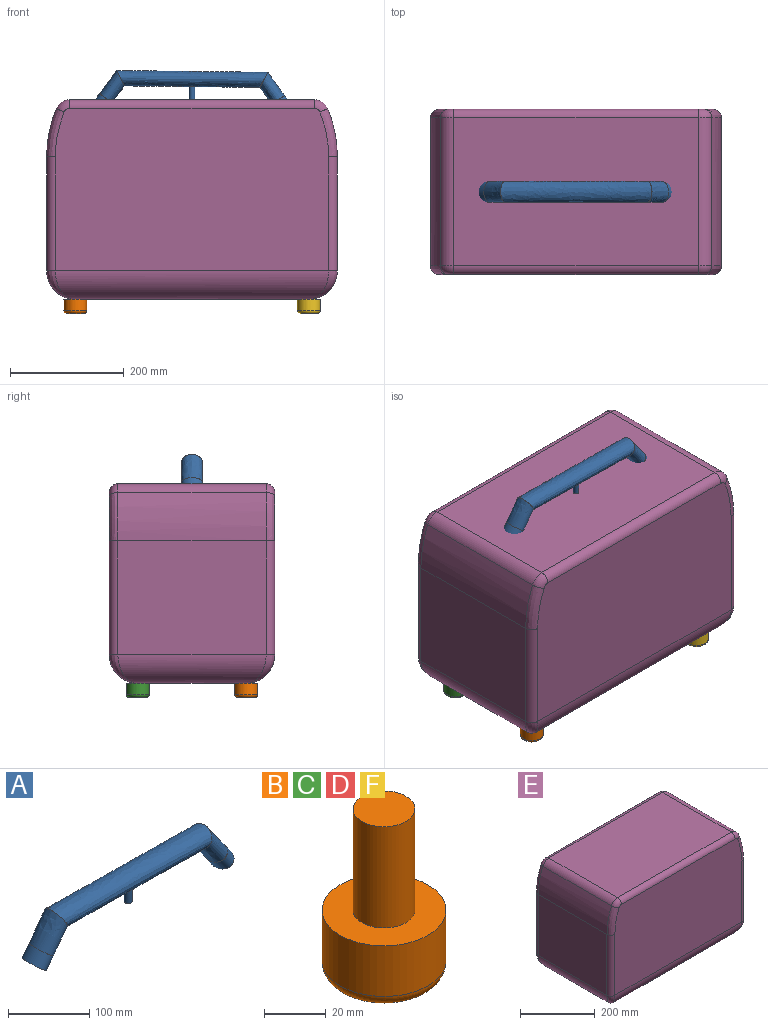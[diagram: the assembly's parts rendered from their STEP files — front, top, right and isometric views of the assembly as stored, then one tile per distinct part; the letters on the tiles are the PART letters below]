
ASSEMBLY  parts=6 mates=5
PART A: 9 faces, bbox 359.2x36.4x84.2 mm
  f0: bspline ~265.3x36.21mm, area 25120.1mm2, adj f3,f5,f7
  f1: plane 36.39x21.71mm, normal (0.59,0,-0.81), area 769.4mm2, adj f4
  f2: plane 36.39x21.24mm, normal (-0.61,0,-0.79), area 769.4mm2, adj f6
  f3: bspline ~56.62x50.7mm, area 4362mm2, adj f0,f4
  f4: bspline ~55.05x48.1mm, area 2003.3mm2, adj f1,f3
  f5: bspline ~56.89x52.04mm, area 4384.8mm2, adj f0,f6
  f6: bspline ~36.21x33.59mm, area 2002mm2, adj f2,f5
  f7: cylinder r=5mm len=23.14mm, axis (0,0,-1), area 727mm2, adj f0,f8
  f8: plane 10x10mm, normal (0,0,-1), area 78.5mm2, adj f7
PART B: 6 faces, bbox 43.3x43.3x65 mm
  f0: cylinder r=20mm len=40mm, axis (0,0,1), area 2513.3mm2, adj f2,f5
  f1: plane 30x30mm, normal (0,0,-1), area 706.9mm2, adj f5
  f2: plane 40x40mm, normal (0,0,1), area 942.5mm2, adj f0,f3
  f3: cylinder r=10mm len=40mm, axis (0,0,-1), area 2513.3mm2, adj f2,f4
  f4: plane 20x20mm, normal (0,0,1), area 314.2mm2, adj f3
  f5: torus R=15mm, axis (0,0,1), area 897.3mm2, adj f0,f1
PART C: same geometry as B
PART D: same geometry as B
PART E: 32 faces, bbox 510x290x350 mm
  f0: plane 260x200mm, normal (1,0,0), area 52000mm2, adj f3,f6,f15,f30
  f1: plane 429.9x260mm, normal (0,0,1), area 111772.7mm2, adj f10,f11,f18,f27
  f2: plane 260x200mm, normal (-1,0,0), area 52000mm2, adj f4,f7,f21,f24
  f3: extruded ~260x84.59mm, area 22577.4mm2, adj f0,f10,f16,f29
  f4: extruded ~260x84.59mm, area 22577.4mm2, adj f2,f11,f20,f25
  f5: plane 410x190mm, normal (0,0,-1), area 77900mm2, adj f6,f7,f9,f13
  f6: cylinder r=50mm len=260mm, axis (0,-1,0), area 18422.6mm2, adj f0,f5,f14,f31
  f7: cylinder r=50mm len=260mm, axis (0,1,0), area 18422.6mm2, adj f2,f5,f22,f23
  f8: plane 480x285mm, normal (0,1,0), area 135753.4mm2, adj f9,f24,f25,f26,f27,f28,f29,f30
  f9: cylinder r=50mm len=480mm, axis (1,0,0), area 35701.3mm2, adj f5,f8,f23,f31
  f10: cylinder r=25mm len=260mm, axis (0,1,0), area 7651mm2, adj f1,f3,f17,f28
  f11: cylinder r=25mm len=260mm, axis (0,1,0), area 7651mm2, adj f1,f4,f19,f26
  f12: plane 480x285mm, normal (0,-1,0), area 135753.4mm2, adj f13,f15,f16,f17,f18,f19,f20,f21
  f13: cylinder r=50mm len=480mm, axis (1,0,0), area 35701.3mm2, adj f5,f12,f14,f22
  f14: bspline ~58.44x50mm, area 1261.4mm2, adj f6,f13,f15
  f15: cylinder r=15mm len=200mm, axis (0,0,1), area 4712.4mm2, adj f0,f12,f14,f16
  f16: bspline ~109.39x35.94mm, area 1995.5mm2, adj f3,f12,f15,f17
  f17: torus R=10mm, axis (0,1,0), area 542.2mm2, adj f10,f12,f16,f18
  f18: cylinder r=15mm len=429.9mm, axis (-1,0,0), area 10129.2mm2, adj f1,f12,f17,f19
  f19: torus R=10mm, axis (0,1,0), area 542.2mm2, adj f11,f12,f18,f20
  f20: bspline ~109.39x35.94mm, area 1995.5mm2, adj f4,f12,f19,f21
  f21: cylinder r=15mm len=200mm, axis (0,0,-1), area 4712.4mm2, adj f2,f12,f20,f22
  f22: bspline ~58.44x50mm, area 1261.4mm2, adj f7,f13,f21
  f23: bspline ~58.44x50mm, area 1261.4mm2, adj f7,f9,f24
  f24: cylinder r=15mm len=200mm, axis (0,0,-1), area 4712.4mm2, adj f2,f8,f23,f25
  f25: bspline ~109.39x35.94mm, area 1995.5mm2, adj f4,f8,f24,f26
  f26: torus R=10mm, axis (0,-1,0), area 542.2mm2, adj f8,f11,f25,f27
  f27: cylinder r=15mm len=429.9mm, axis (-1,0,0), area 10129.2mm2, adj f1,f8,f26,f28
  f28: torus R=10mm, axis (0,-1,0), area 542.2mm2, adj f8,f10,f27,f29
  f29: bspline ~109.39x35.94mm, area 1995.5mm2, adj f3,f8,f28,f30
  f30: cylinder r=15mm len=200mm, axis (0,0,1), area 4712.4mm2, adj f0,f8,f29,f31
  f31: bspline ~58.44x50mm, area 1261.4mm2, adj f6,f9,f30
PART F: same geometry as B
PLACE A t=(-243.46,-56.64,300.88)mm
PLACE B t=(-448.46,-151.64,-49.12)mm
PLACE C t=(-448.46,38.36,-49.12)mm
PLACE D t=(-38.46,38.36,-49.12)mm
PLACE E t=(-243.46,-56.64,100.88)mm fixed
PLACE F t=(-38.46,-151.64,-49.12)mm
MATE fastened A.f7 <-> E.f1  axis (0,0,-1) through (-243.46,-56.64,300.88)mm
MATE fastened D.f3 <-> E.f5  axis (0,0,-1) through (-38.46,38.36,-49.12)mm
MATE fastened F.f3 <-> E.f5  axis (0,0,-1) through (-38.46,-151.64,-49.12)mm
MATE fastened B.f3 <-> E.f5  axis (0,0,1) through (-448.46,-151.64,-49.12)mm
MATE fastened C.f3 <-> E.f5  axis (0,0,-1) through (-448.46,38.36,-49.12)mm
